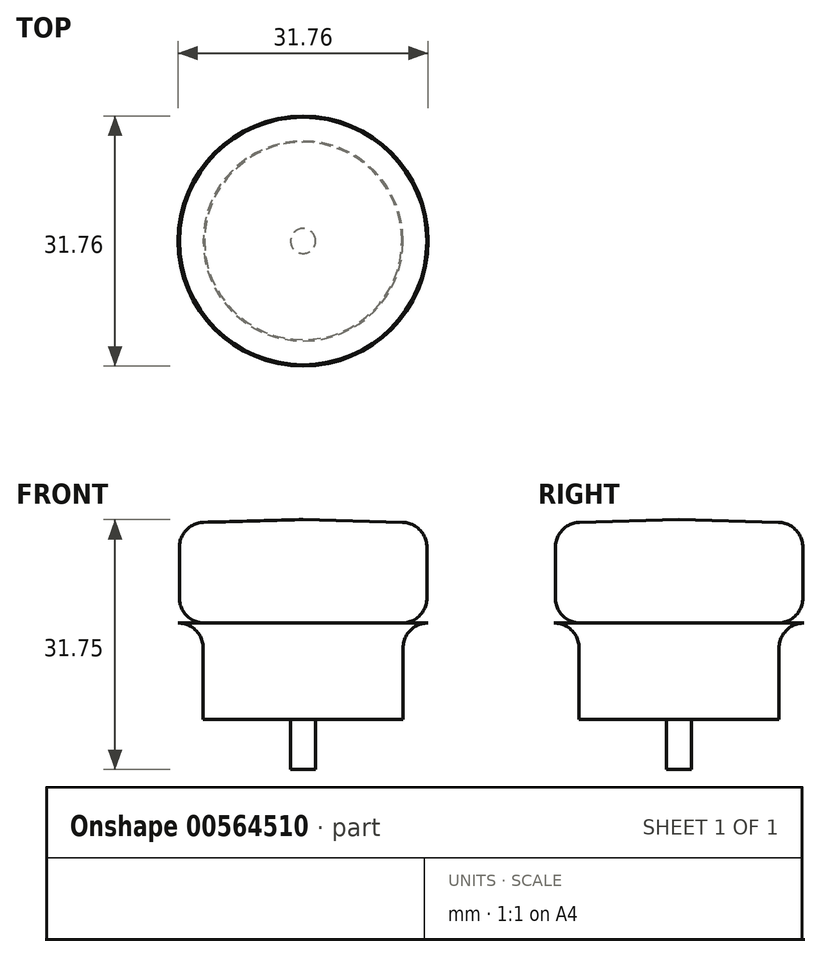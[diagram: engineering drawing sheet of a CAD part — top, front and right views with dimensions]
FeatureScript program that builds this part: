
annotation { "Feature Type Name" : "Feature", "Feature Type Description" : "" }
export const myFeature = defineFeature(function(context is Context, id is Id, definition is map)
    precondition{}
    {
        {
            var Q0;
            Q0=qCreatedBy(makeId("Front.planeOp"),FACE);
            var sketch = newSketch(context, id + "F0", { "sketchPlane" : qUnion([Q0])});
            skLineSegment(sketch, "E0.top", {"start": v(0, 15.34) * mm, "end": v(-12.7, 15.34) * mm});
            skLineSegment(sketch, "E0.left", {"start": v(0, 40.74) * mm, "end": v(0, 15.34) * mm});
            skLineSegment(sketch, "E0.right", {"start": v(-12.7, 24.42) * mm, "end": v(-12.7, 15.34) * mm});
            skPoint(sketch, "E1.visualSharp", {"position": v(-12.7, 78.84) * mm});
            skLineSegment(sketch, "E2", {"start": v(-12.54, 27.6) * mm, "end": v(-15.87, 27.6) * mm});
            skLineSegment(sketch, "E3", {"start": v(-15.72, 30.77) * mm, "end": v(-15.72, 37.21) * mm});
            skLineSegment(sketch, "E4", {"start": v(-12.63, 40.39) * mm, "end": v(0, 40.74) * mm});
            skPoint(sketch, "E5.visualSharp", {"position": v(-15.72, 27.6) * mm});
            skArc(sketch, "E5.filletArc", {"start": v(-15.72, 30.77) * mm, "mid": v(-14.79, 28.53) * mm, "end": v(-12.54, 27.6) * mm});
            skPoint(sketch, "E6.visualSharp", {"position": v(-15.72, 40.3) * mm});
            skArc(sketch, "E6.filletArc", {"start": v(-12.63, 40.39) * mm, "mid": v(-14.82, 39.42) * mm, "end": v(-15.72, 37.21) * mm});
            skPoint(sketch, "E7.visualSharp", {"position": v(-12.7, 27.6) * mm});
            skArc(sketch, "E7.filletArc", {"start": v(-12.7, 24.42) * mm, "mid": v(-13.63, 26.67) * mm, "end": v(-15.87, 27.6) * mm});
            skSolve(sketch);
        }
        {
            var Q0;
            Q0=makeQuery(id+"F0.imprint","IMPRINT",FACE,{"disambiguationData":[TD([[makeQuery(id+"F0.imprint","IMPRINT",EDGE,{"derivedFrom":sQuery(id+"F0.wireOp",EDGE,"E0.top")}),-1.0]])]});
            var Q1;
            Q1=sQuery(id+"F0.wireOp",EDGE,"E0.left");
            revolve(context, id + "F1", {"entities" : qUnion([Q0]), "axis" : qUnion([Q1]), "revolveType" : RevolveType.FULL});
        }
        {
            var Q0;
            Q0=makeQuery(id+"F1.opRevolve","SWEPT_FACE",FACE,{"disambiguationData":[OSD([sQuery(id+"F0.wireOp",EDGE,"E0.top")])]});
            var sketch = newSketch(context, id + "F2", { "sketchPlane" : qUnion([Q0])});
            skCircle(sketch, "E8", {"center": v(0, 0) * mm, "radius": 1.59 * mm});
            skSolve(sketch);
        }
        {
            var Q0;
            Q0=makeQuery(id+"F2.imprint","IMPRINT",FACE,{"disambiguationData":[TD([[makeQuery(id+"F2.imprint","IMPRINT",EDGE,{"derivedFrom":sQuery(id+"F2.wireOp",EDGE,"E8")}),1.0]])]});
            var Q1;
            Q1=sQuery(id+"F2.wireOp",EDGE,"E8");
            extrude(context, id + "F3", {"entities" : qUnion([Q0]), "operationType" : NewBodyOperationType.ADD, "surfaceEntities" : qUnion([Q1]), "depth" : 6.35 * mm, "offsetDistance" : 25.4 * mm});
        }
    });
